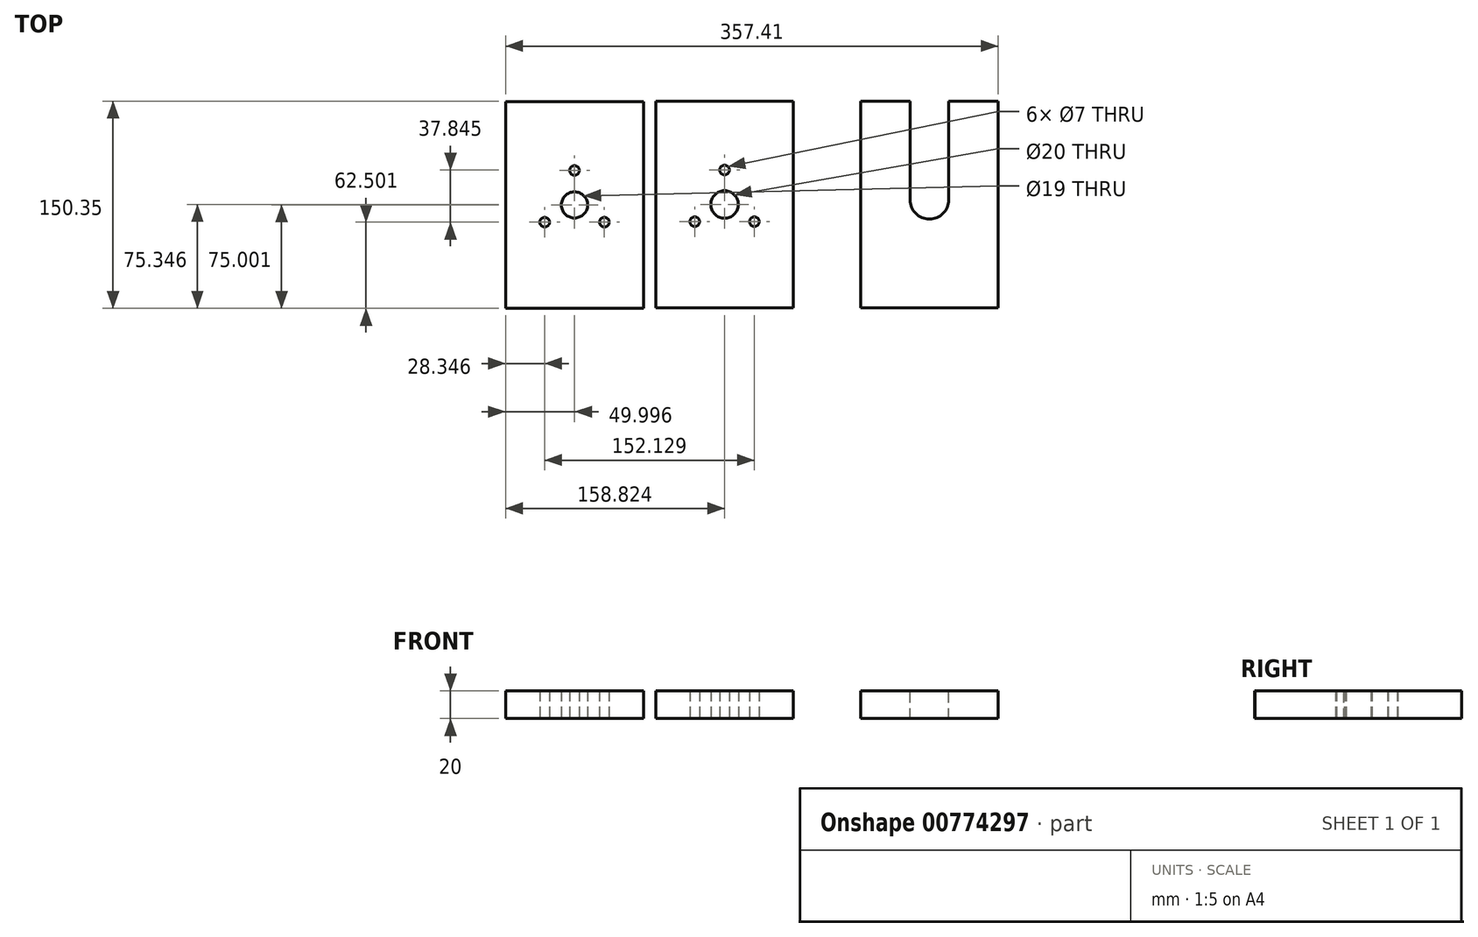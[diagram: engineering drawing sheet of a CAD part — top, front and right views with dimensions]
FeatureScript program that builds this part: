
annotation { "Feature Type Name" : "Feature", "Feature Type Description" : "" }
export const myFeature = defineFeature(function(context is Context, id is Id, definition is map)
    precondition{}
    {
        {
            var Q0;
            Q0=qCreatedBy(makeId("Top.planeOp"),FACE);
            var sketch = newSketch(context, id + "F0", { "sketchPlane" : qUnion([Q0])});
            skLineSegment(sketch, "E0", {"start": v(-28.29, -27.53) * mm, "end": v(71.71, -27.53) * mm});
            skLineSegment(sketch, "E1", {"start": v(71.71, 122.47) * mm, "end": v(-28.29, 122.47) * mm});
            skLineSegment(sketch, "E2", {"start": v(-28.29, 122.47) * mm, "end": v(-28.29, -27.53) * mm});
            skCircle(sketch, "E3", {"center": v(21.71, 47.47) * mm, "radius": 10 * mm});
            skLineSegment(sketch, "E4", {"start": v(71.71, -27.53) * mm, "end": v(71.71, 122.47) * mm});
            skCircle(sketch, "E5", {"center": v(21.71, 72.47) * mm, "radius": 3.5 * mm});
            skCircle(sketch, "E6.1.0", {"center": v(0.06, 34.97) * mm, "radius": 3.5 * mm});
            skCircle(sketch, "E6.2.0", {"center": v(43.36, 34.97) * mm, "radius": 3.5 * mm});
            skLineSegment(sketch, "E7", {"start": v(-137.11, -27.88) * mm, "end": v(-37.11, -27.88) * mm});
            skLineSegment(sketch, "E8", {"start": v(-37.11, 122.12) * mm, "end": v(-137.11, 122.12) * mm});
            skLineSegment(sketch, "E9", {"start": v(-137.11, 122.12) * mm, "end": v(-137.11, -27.88) * mm});
            skCircle(sketch, "E10", {"center": v(-87.11, 47.12) * mm, "radius": 9.5 * mm});
            skLineSegment(sketch, "E11", {"start": v(-37.11, -27.88) * mm, "end": v(-37.11, 122.12) * mm});
            skCircle(sketch, "E12", {"center": v(-87.11, 72.12) * mm, "radius": 3.5 * mm});
            skCircle(sketch, "E13.1.0", {"center": v(-108.76, 34.62) * mm, "radius": 3.5 * mm});
            skCircle(sketch, "E13.2.0", {"center": v(-65.46, 34.62) * mm, "radius": 3.5 * mm});
            skLineSegment(sketch, "E14.MirrorCS", {"start": v(120.3, -27.53) * mm, "end": v(120.3, 122.47) * mm});
            skLineSegment(sketch, "E15.MirrorCS", {"start": v(220.3, 122.47) * mm, "end": v(220.3, -27.53) * mm});
            skLineSegment(sketch, "E16.MirrorCS", {"start": v(120.3, 122.47) * mm, "end": v(220.3, 122.47) * mm});
            skLineSegment(sketch, "E17.MirrorCS", {"start": v(220.3, -27.53) * mm, "end": v(120.3, -27.53) * mm});
            skSolve(sketch);
        }
        {
            var Q0;
            Q0 = qSketchRegion(id + "F0", true);
            extrude(context, id + "F1", {"entities" : qUnion([Q0]), "depth" : 20 * mm, "offsetDistance" : 25 * mm});
        }
        {
            var Q0;
            Q0=makeQuery(id+"F1.opExtrude","SWEPT_FACE",FACE,{"disambiguationData":[OSD([sQuery(id+"F0.wireOp",EDGE,"E16.MirrorCS")])]});
            var sketch = newSketch(context, id + "F2", { "sketchPlane" : qUnion([Q0])});
            skLineSegment(sketch, "E18", {"start": v(-170.3, 0) * mm, "end": v(-170.3, 20) * mm});
            skLineSegment(sketch, "E19", {"start": v(-184.3, 0) * mm, "end": v(-184.3, 20) * mm});
            skLineSegment(sketch, "E20", {"start": v(-156.3, 0) * mm, "end": v(-156.3, 20) * mm});
            skLineSegment(sketch, "E21", {"start": v(-156.3, 20) * mm, "end": v(-184.3, 20) * mm});
            skLineSegment(sketch, "E22", {"start": v(-156.3, 0) * mm, "end": v(-184.3, 0) * mm});
            skSolve(sketch);
        }
        {
            var Q0;
            Q0 = qSketchRegion(id + "F2", true);
            extrude(context, id + "F3", {"entities" : qUnion([Q0]), "operationType" : NewBodyOperationType.REMOVE, "oppositeDirection" : true, "depth" : 71.55 * mm, "offsetDistance" : 25 * mm});
        }
        {
            var Q0;
            Q0=makeQuery(id+"F1.opExtrude","CAP_FACE",FACE,{"disambiguationData":[OSD([sQuery(id+"F0.wireOp",EDGE,"E14.MirrorCS"),sQuery(id+"F0.wireOp",EDGE,"E15.MirrorCS"),sQuery(id+"F0.wireOp",EDGE,"E16.MirrorCS"),sQuery(id+"F0.wireOp",EDGE,"E17.MirrorCS")])],"isStart":false});
            var sketch = newSketch(context, id + "F4", { "sketchPlane" : qUnion([Q0])});
            skArc(sketch, "E23", {"start": v(156.3, 50.92) * mm, "mid": v(170.3, 36.92) * mm, "end": v(184.3, 50.92) * mm});
            skLineSegment(sketch, "E24", {"start": v(156.3, 50.92) * mm, "end": v(184.3, 50.92) * mm});
            skSolve(sketch);
        }
        {
            var Q0;
            Q0 = qSketchRegion(id + "F4", true);
            extrude(context, id + "F5", {"entities" : qUnion([Q0]), "operationType" : NewBodyOperationType.REMOVE, "oppositeDirection" : true, "depth" : 25 * mm, "offsetDistance" : 25 * mm});
        }
    });
